# Revit family: FWE_2014
name_source: partatom
category: Specialty Equipment
revit_build: Autodesk Revit 2014 (Build: 20130308_1515(x64)
units: mm (PartAtom-declared; Revit-internal decimal feet)

## types (1)
- FWE_2014
    Bumper = Extruded PVC - 701 Black
    Case = Textured Sheet Metal (Steel Painted) - 149 White Satin Matte
    Case Interior = Sheet Metal (Steel Painted) - 700 Interior White
    Case Weight = 500.00 lbf
    Cutsheet URL = http://www.hussmann.com
    Depth = 42"
    Description = Wide Island Merchandiser for Frozen Food / Ice Cream End Case
    End Weight = 0.00 lbf
    Ends = Textured Sheet Metal (Steel Painted) - 149 White Satin Matte
    Height = 35 7/8"
    Manufacturer = Hussmann Corporation
    Manufacturer Disclaimer = The information in this file is not intended to be an exact representation of the corresponding Hussmann product.  Further, we reserve the right to change or revise specifications and product design in connection with any feature of our products. Such changes do not entitle the buyer to corresponding changes, improvements, additions, or replacements for equipment previously sold or shipped.
    Model = FWE
    Model URL = http://www.hussmann.com
    Note from Manufacturer = This model only comes in this length.
    Number of Supports = 2
    Refrig. Liquid = Liquid
    Refrig. Suction = Suction
    Refrigeration Lines Liquid = 3/8"
    Refrigeration Lines Suction = 5/8"
    Revit Family Date = 02/19/2016
    Splashguard = Textured Sheet Metal (Steel Painted) - 701 Black
    Total Weight = 500.00 lbf
    Trim = Plastic - 144 Mist Gray
    Type Comments = Excel
    URL = www.hussmann.com
    Waste Drain = 1 1/4"
    Width = 80 5/8"

## geometry (parser evidence)
native form markers: Sweep x8
no freeform markers — native parametric forms only
